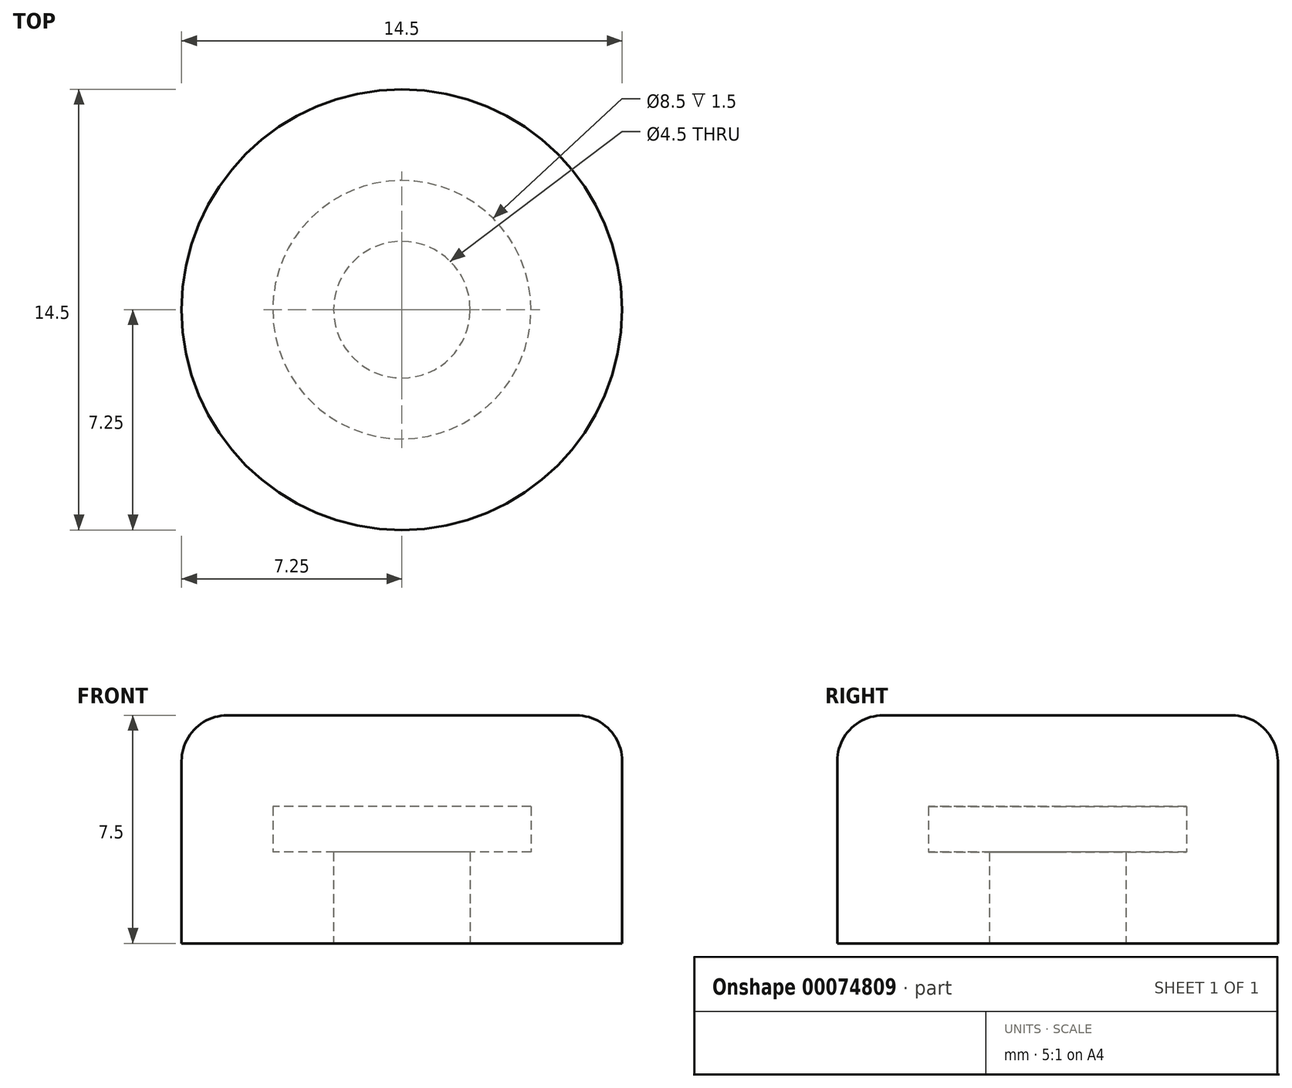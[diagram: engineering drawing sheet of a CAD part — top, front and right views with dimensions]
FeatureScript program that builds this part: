
annotation { "Feature Type Name" : "Feature", "Feature Type Description" : "" }
export const myFeature = defineFeature(function(context is Context, id is Id, definition is map)
    precondition{}
    {
        {
            assignVariable(context, id + "F0", {"name" : "HeadDepth", "anyValue" : 2.5});
        }
        {
            assignVariable(context, id + "F1", {"name" : "PrintingOffset", "anyValue" : .5});
        }
        {
            assignVariable(context, id + "F2", {"name" : "WallThickness", "anyValue" : 3});
        }
        {
            assignVariable(context, id + "F3", {"name" : "Height", "anyValue" : getVariable(context, 'HeadDepth') + (getVariable(context, 'WallThickness') * 1.5) + getVariable(context, 'PrintingOffset')});
        }
        {
            var Q0;
            Q0=qCreatedBy(makeId("Top.planeOp"),FACE);
            var sketch = newSketch(context, id + "F4", { "sketchPlane" : qUnion([Q0])});
            skCircle(sketch, "E0", {"center": v(0, 0) * mm, "radius": 2.25 * mm});
            skCircle(sketch, "E1", {"center": v(0, 0) * mm, "radius": 4.25 * mm});
            skCircle(sketch, "E2.0", {"center": v(0, 0) * mm, "radius": 7.25 * mm});
            skSolve(sketch);
        }
        {
            var Q0;
            Q0 = qSketchRegion(id + "F4", true);
            extrude(context, id + "F5", {"entities" : qUnion([Q0]), "depth" : (getVariable(context, 'Height')) * mm});
        }
        {
            var Q0;
            Q0=makeQuery(id+"F4.imprint","IMPRINT",FACE,{"disambiguationData":[TD([[makeQuery(id+"F4.imprint","IMPRINT",EDGE,{"derivedFrom":sQuery(id+"F4.wireOp",EDGE,"E0")}),-1.0]])]});
            extrude(context, id + "F6", {"entities" : qUnion([Q0]), "operationType" : NewBodyOperationType.ADD, "depth" : (getVariable(context, 'WallThickness')) * mm});
        }
        {
            var Q0;
            Q0=makeQuery(id+"F5.opExtrude","CAP_EDGE",EDGE,{"disambiguationData":[OSD([sQuery(id+"F4.wireOp",EDGE,"E2.0")])],"isStart":false});
            fillet(context, id + "F7", {"entities" : qUnion([Q0]), "radius" : (getVariable(context, 'WallThickness') / 2) * mm, "tangentPropagation" : true, "allowEdgeOverflow" : false});
        }
        {
            var Q0;
            Q0=makeQuery(id+"F4.imprint","IMPRINT",FACE,{"disambiguationData":[TD([[makeQuery(id+"F4.imprint","IMPRINT",EDGE,{"derivedFrom":sQuery(id+"F4.wireOp",EDGE,"E0")}),-1.0]])]});
            var Q1;
            Q1=makeQuery(id+"F4.imprint","IMPRINT",FACE,{"disambiguationData":[TD([[makeQuery(id+"F4.imprint","IMPRINT",EDGE,{"derivedFrom":sQuery(id+"F4.wireOp",EDGE,"E0")}),1.0]])]});
            extrude(context, id + "F8", {"entities" : qUnion([Q0, Q1]), "operationType" : NewBodyOperationType.ADD, "depth" : (getVariable(context, 'Height')) * mm, "hasSecondDirection" : true, "secondDirectionOppositeDirection" : false, "secondDirectionDepth" : (getVariable(context, 'Height') - getVariable(context, 'WallThickness')) * mm});
        }
    });
